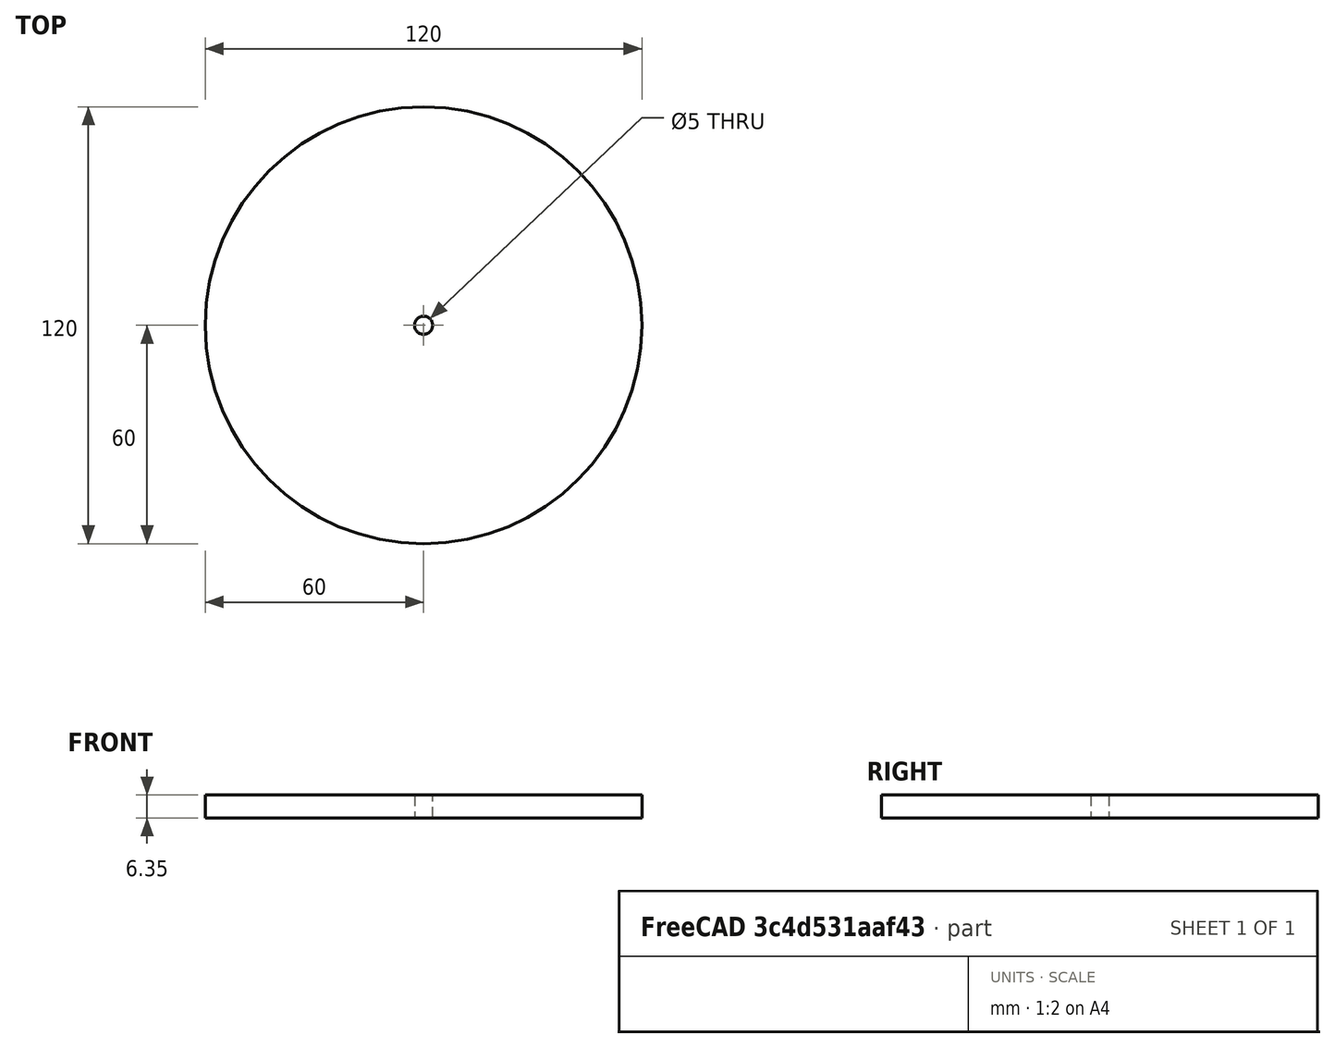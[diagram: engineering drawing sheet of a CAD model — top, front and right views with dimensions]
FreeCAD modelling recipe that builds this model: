
FCSTD DOCUMENT  (FreeCAD 0.20R29177 +426 (Git))
Label: Wheel
License: All rights reserved
LicenseURL: http://en.wikipedia.org/wiki/All_rights_reserved
objects: App::DocumentObjectGroup×3, PartDesign::CoordinateSystem×1, App::FeaturePython×1, Sketcher::SketchObject×1, PartDesign::Pad×1, PartDesign::Body×1, App::Part×1
note: 5 computed .brp shape members not serialized (recipe doc carries the construction recipe); baked Part::Feature solids carry a one-line shape summary decoded from their .brp

FEATURE [App::DocumentObjectGroup] Parts
FEATURE [PartDesign::CoordinateSystem] LCS_Origin
  AttacherType = Attacher::AttachEngine3D
  MapMode = 2
  Support = -> [X_Axis]
FEATURE [App::DocumentObjectGroup] Constraints
FEATURE [App::FeaturePython] Variables  # WARN: FeaturePython — macro-defined, semantics opaque (R4)
  Type = App::PropertyContainer
FEATURE [App::DocumentObjectGroup] Configurations
FEATURE [Sketcher::SketchObject] Sketch
  FullyConstrained = true
  MapMode = 5
  Support = -> [XY_Plane001]
  sketch-geometry (2):
    g0: Circle CenterX=0 CenterY=0 CenterZ=0 NormalX=0 NormalY=0 NormalZ=1 AngleXU=0 Radius=60
    g1: Circle CenterX=0 CenterY=0 CenterZ=0 NormalX=0 NormalY=0 NormalZ=1 AngleXU=0 Radius=2.5
  constraints (4):
    c: Coincident(g0,g-1)
    c: Diameter(g0) = 120
    c: Coincident(g1,g0)
    c: Diameter(g1) = 5
FEATURE [PartDesign::Pad] Pad
  Direction = (0,0,1)
  Length = 6.35
  Length2 = 10
  Profile = -> Sketch
  ReferenceAxis = -> Sketch [N_Axis]
  Type = 0
FEATURE [PartDesign::Body] Body
  Group = -> [Sketch,Pad]
  Origin = -> Origin001
  Tip = -> Pad
FEATURE [App::Part] Assembly
  AssemblyType = Part::Link
  Group = -> [LCS_Origin,Constraints,Variables,Configurations,Body]
  Origin = -> Origin
  Type = Assembly
